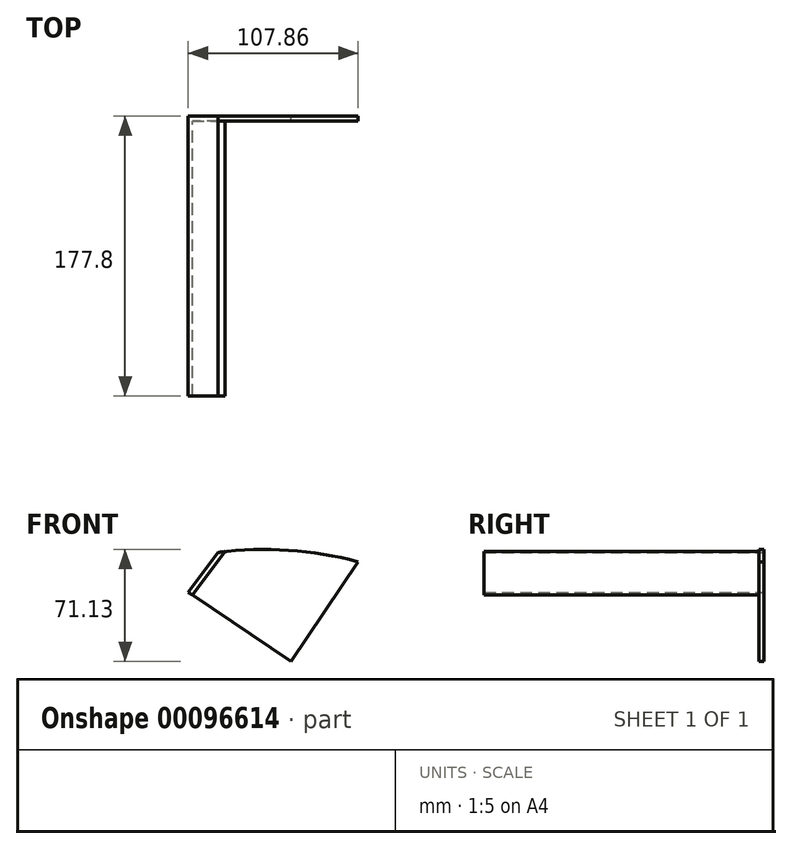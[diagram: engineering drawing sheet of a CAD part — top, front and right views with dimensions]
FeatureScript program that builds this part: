
annotation { "Feature Type Name" : "Feature", "Feature Type Description" : "" }
export const myFeature = defineFeature(function(context is Context, id is Id, definition is map)
    precondition{}
    {
        {
            var Q0;
            Q0=qCreatedBy(makeId("Front.planeOp"),FACE);
            var sketch = newSketch(context, id + "F0", { "sketchPlane" : qUnion([Q0])});
            skCircle(sketch, "E0", {"center": v(0, 0) * mm, "radius": 228.6 * mm});
            skLineSegment(sketch, "E1", {"start": v(59.4, 220.75) * mm, "end": v(20.5, 162.74) * mm});
            skLineSegment(sketch, "E2", {"start": v(11.68, 161) * mm, "end": v(-42.9, 197.62) * mm});
            skLineSegment(sketch, "E3", {"start": v(-44.45, 206.7) * mm, "end": v(-29.47, 226.7) * mm});
            skPoint(sketch, "E4.visualSharp", {"position": v(-48.46, 201.35) * mm});
            skPoint(sketch, "E5.visualSharp", {"position": v(16.95, 157.47) * mm});
            skLineSegment(sketch, "E6", {"start": v(-44.45, 206.7) * mm, "end": v(-48.46, 201.35) * mm});
            skLineSegment(sketch, "E7", {"start": v(-42.9, 197.62) * mm, "end": v(-48.46, 201.35) * mm});
            skLineSegment(sketch, "E8", {"start": v(20.5, 162.74) * mm, "end": v(16.95, 157.47) * mm});
            skLineSegment(sketch, "E9", {"start": v(11.68, 161) * mm, "end": v(16.95, 157.47) * mm});
            skSolve(sketch);
        }
        {
            var Q0;
            {var subQ1=sQuery(id+"F0.wireOp",EDGE,"E1");Q0=makeQuery(id+"F0.imprint","IMPRINT",FACE,{"disambiguationData":[TD([[makeQuery(id+"F0.imprint","IMPRINT",EDGE,{"derivedFrom":subQ1}),-1.0]])]});}
            extrude(context, id + "F1", {"entities" : qUnion([Q0]), "depth" : 3.17 * mm});
        }
        {
            var Q0;
            Q0=makeQuery(id+"F1.opExtrude","CAP_FACE",FACE,{"disambiguationData":[OSD([sQuery(id+"F0.wireOp",EDGE,"E0"),sQuery(id+"F0.wireOp",EDGE,"E1"),sQuery(id+"F0.wireOp",EDGE,"E2"),sQuery(id+"F0.wireOp",EDGE,"E3"),sQuery(id+"F0.wireOp",EDGE,"E6"),sQuery(id+"F0.wireOp",EDGE,"E7"),sQuery(id+"F0.wireOp",EDGE,"E8"),sQuery(id+"F0.wireOp",EDGE,"E9")])],"isStart":true});
            var sketch = newSketch(context, id + "F2", { "sketchPlane" : qUnion([Q0])});
            skLineSegment(sketch, "E10", {"start": v(29.47, 226.7) * mm, "end": v(48.46, 201.35) * mm});
            skLineSegment(sketch, "E11", {"start": v(48.46, 201.35) * mm, "end": v(-16.95, 157.47) * mm});
            skLineSegment(sketch, "E12", {"start": v(-16.95, 157.47) * mm, "end": v(-59.4, 220.75) * mm});
            skLineSegment(sketch, "E13", {"start": v(-59.4, 220.75) * mm, "end": v(-16.95, 157.47) * mm});
            skArc(sketch, "E14", {"start": v(29.47, 226.7) * mm, "mid": v(-15.26, 228.08) * mm, "end": v(-59.4, 220.75) * mm});
            skLineSegment(sketch, "E15", {"start": v(29.47, 226.7) * mm, "end": v(26.96, 224.81) * mm});
            skLineSegment(sketch, "E16", {"start": v(26.96, 224.81) * mm, "end": v(45.86, 199.6) * mm});
            skLineSegment(sketch, "E17", {"start": v(45.86, 199.6) * mm, "end": v(25.16, 227.2) * mm});
            skLineSegment(sketch, "E18", {"start": v(25.16, 227.2) * mm, "end": v(45.86, 199.6) * mm});
            skLineSegment(sketch, "E19", {"start": v(-16.95, 157.47) * mm, "end": v(-14.5, 159.12) * mm});
            skLineSegment(sketch, "E20", {"start": v(-14.5, 159.12) * mm, "end": v(-56.37, 221.54) * mm});
            skLineSegment(sketch, "E21", {"start": v(-56.37, 221.54) * mm, "end": v(-14.5, 159.12) * mm});
            skLineSegment(sketch, "E22", {"start": v(-16.95, 157.47) * mm, "end": v(-18.75, 160.15) * mm});
            skLineSegment(sketch, "E23", {"start": v(-18.75, 160.15) * mm, "end": v(46.52, 203.93) * mm});
            skLineSegment(sketch, "E24", {"start": v(46.52, 203.93) * mm, "end": v(-18.75, 160.15) * mm});
            skSolve(sketch);
        }
        {
            var Q0;
            {var subQ1=sQuery(id+"F2.wireOp",EDGE,"E11");var subQ3=sQuery(id+"F2.wireOp",EDGE,"E18");var subQ4=makeQuery(id+"F2.imprint","INTERSECT",VERTEX,{"derivedFrom":[subQ1,subQ3]});Q0=makeQuery(id+"F2.imprint","IMPRINT",FACE,{"disambiguationData":[TD([[makeQuery(id+"F2.imprint","IMPRINT",EDGE,{"disambiguationData":[TD([[subQ4,1.0]])],"derivedFrom":subQ3}),-1.0]])]});}
            var Q1;
            {var subQ0=sQuery(id+"F2.wireOp",EDGE,"E19");Q1=makeQuery(id+"F2.imprint","IMPRINT",FACE,{"disambiguationData":[TD([[makeQuery(id+"F2.imprint","IMPRINT",EDGE,{"derivedFrom":subQ0}),1.0]])]});}
            var Q2;
            {var subQ0=sQuery(id+"F2.wireOp",EDGE,"E13");Q2=makeQuery(id+"F2.imprint","IMPRINT",FACE,{"disambiguationData":[TD([[makeQuery(id+"F2.imprint","IMPRINT",EDGE,{"derivedFrom":subQ0}),1.0]])]});}
            var Q3;
            {var subQ0=sQuery(id+"F2.wireOp",EDGE,"E11");var subQ1=sQuery(id+"F2.wireOp",EDGE,"E10");var subQ2=makeQuery(id+"F2.imprint","INTERSECT",VERTEX,{"derivedFrom":[subQ1,subQ0]});Q3=makeQuery(id+"F2.imprint","IMPRINT",FACE,{"disambiguationData":[TD([[makeQuery(id+"F2.imprint","IMPRINT",EDGE,{"disambiguationData":[TD([[subQ2,-1.0]])],"derivedFrom":subQ1}),1.0]])]});}
            var Q4;
            {var subQ0=sQuery(id+"F2.wireOp",EDGE,"E15");Q4=makeQuery(id+"F2.imprint","IMPRINT",FACE,{"disambiguationData":[TD([[makeQuery(id+"F2.imprint","IMPRINT",EDGE,{"derivedFrom":subQ0}),1.0]])]});}
            var Q5;
            {var subQ0=sQuery(id+"F2.wireOp",EDGE,"E15");Q5=makeQuery(id+"F2.imprint","IMPRINT",FACE,{"disambiguationData":[TD([[makeQuery(id+"F2.imprint","IMPRINT",EDGE,{"derivedFrom":subQ0}),-1.0]])]});}
            extrude(context, id + "F3", {"entities" : qUnion([Q0, Q1, Q2, Q3, Q4, Q5]), "operationType" : NewBodyOperationType.ADD, "oppositeDirection" : true, "depth" : 177.8 * mm});
        }
    });
